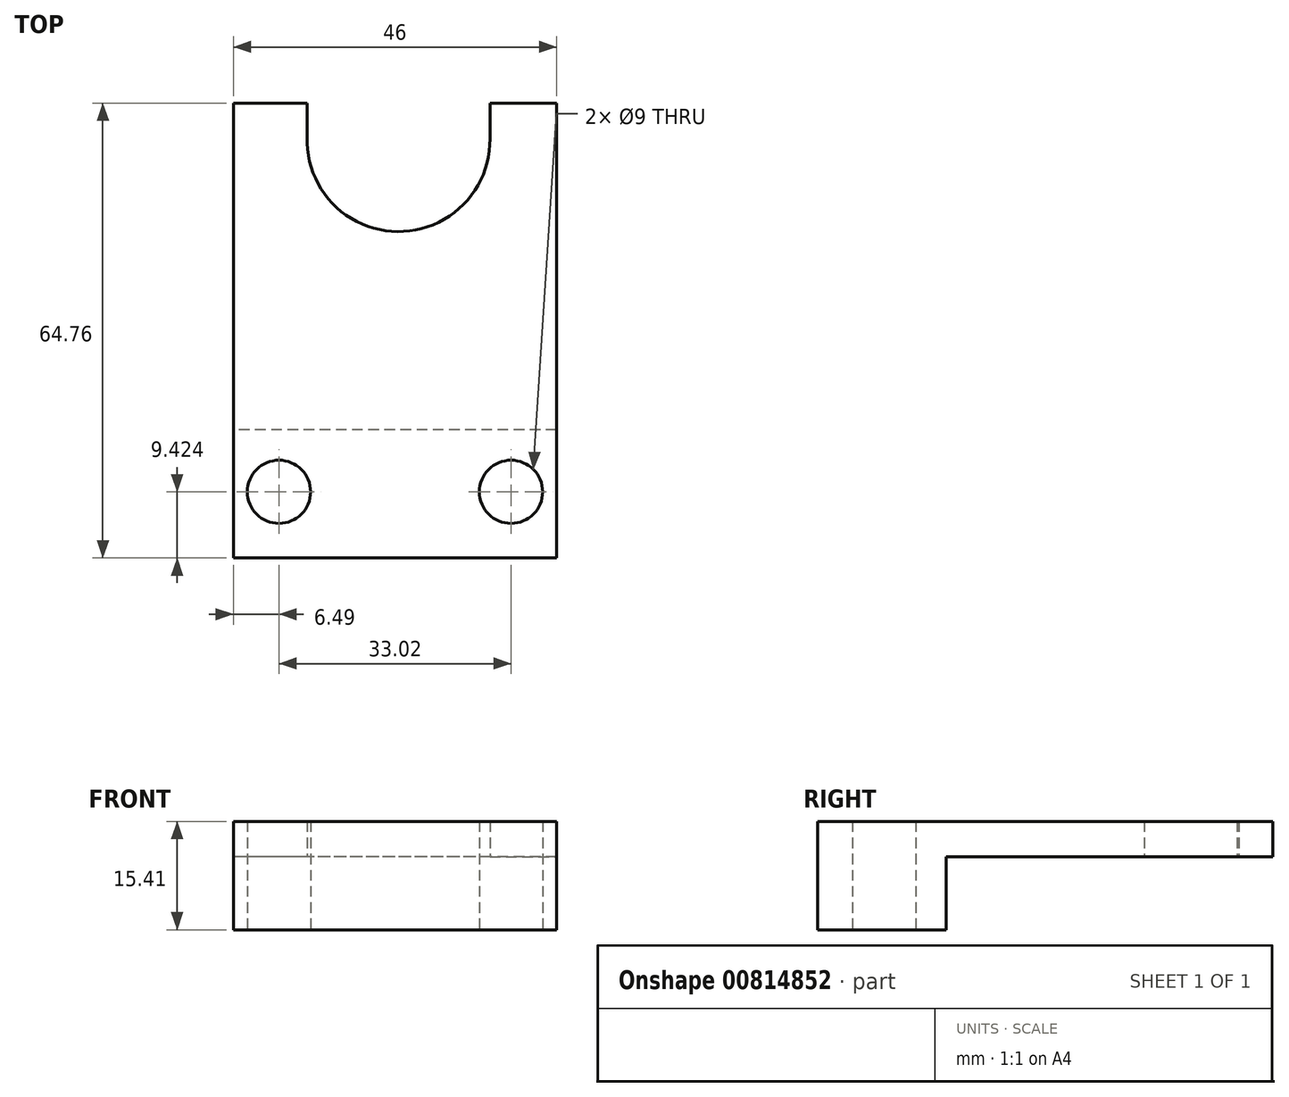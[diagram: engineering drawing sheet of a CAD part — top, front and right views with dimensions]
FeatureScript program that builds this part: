
annotation { "Feature Type Name" : "Feature", "Feature Type Description" : "" }
export const myFeature = defineFeature(function(context is Context, id is Id, definition is map)
    precondition{}
    {
        {
            var Q0;
            Q0=qCreatedBy(makeId("Top.planeOp"),FACE);
            var sketch = newSketch(context, id + "F0", { "sketchPlane" : qUnion([Q0])});
            skLineSegment(sketch, "E0.bottom", {"start": v(23, 53) * mm, "end": v(-23, 53) * mm});
            skLineSegment(sketch, "E0.top", {"start": v(23, -53) * mm, "end": v(-23, -53) * mm});
            skLineSegment(sketch, "E0.left", {"start": v(23, 53) * mm, "end": v(23, -53) * mm});
            skLineSegment(sketch, "E0.right", {"start": v(-23, 53) * mm, "end": v(-23, -53) * mm});
            skPoint(sketch, "E0.middle", {"position": v(0, 0) * mm});
            skArc(sketch, "E1", {"start": v(-1.85, 19.91) * mm, "mid": v(-20, 0.06) * mm, "end": v(-1.97, -19.9) * mm});
            skArc(sketch, "E2", {"start": v(2.22, 19.88) * mm, "mid": v(0.19, 20) * mm, "end": v(-1.85, 19.91) * mm});
            skArc(sketch, "E3", {"start": v(-1.97, -19.9) * mm, "mid": v(0.04, -20) * mm, "end": v(2.05, -19.9) * mm});
            skArc(sketch, "E4", {"start": v(2.05, -19.9) * mm, "mid": v(20, -0.09) * mm, "end": v(2.22, 19.88) * mm});
            skArc(sketch, "E5", {"start": v(-2.06, -20.9) * mm, "mid": v(0, -21) * mm, "end": v(2.06, -20.9) * mm});
            skArc(sketch, "E6", {"start": v(2.06, -20.9) * mm, "mid": v(21, -0.1) * mm, "end": v(2.24, 20.88) * mm});
            skArc(sketch, "E7", {"start": v(-1.88, 20.92) * mm, "mid": v(-21, 0.1) * mm, "end": v(-2.06, -20.9) * mm});
            skArc(sketch, "E8", {"start": v(2.24, 20.88) * mm, "mid": v(0.18, 21) * mm, "end": v(-1.88, 20.92) * mm});
            skLineSegment(sketch, "E9", {"start": v(-1.97, -19.9) * mm, "end": v(-2.06, -20.9) * mm});
            skLineSegment(sketch, "E10", {"start": v(2.05, -19.9) * mm, "end": v(2.06, -20.9) * mm});
            skLineSegment(sketch, "E11", {"start": v(2.24, 20.88) * mm, "end": v(2.22, 19.88) * mm});
            skLineSegment(sketch, "E12", {"start": v(-1.88, 20.92) * mm, "end": v(-1.85, 19.91) * mm});
            skPoint(sketch, "E13", {"position": v(0, -21) * mm});
            skPoint(sketch, "E13.positionSnap0", {"position": v(0, -21) * mm});
            skPoint(sketch, "E14", {"position": v(0.18, 21) * mm});
            skSolve(sketch);
        }
        {
            var Q0;
            Q0=makeQuery(id+"F0.imprint","IMPRINT",FACE,{"disambiguationData":[TD([[makeQuery(id+"F0.imprint","IMPRINT",EDGE,{"derivedFrom":sQuery(id+"F0.wireOp",EDGE,"E1")}),1.0]])]});
            var Q1;
            Q1=makeQuery(id+"F0.imprint","IMPRINT",FACE,{"disambiguationData":[TD([[makeQuery(id+"F0.imprint","IMPRINT",EDGE,{"derivedFrom":sQuery(id+"F0.wireOp",EDGE,"E1")}),-1.0]])]});
            var Q2;
            Q2=makeQuery(id+"F0.imprint","IMPRINT",FACE,{"disambiguationData":[TD([[makeQuery(id+"F0.imprint","IMPRINT",EDGE,{"derivedFrom":sQuery(id+"F0.wireOp",EDGE,"E3")}),-1.0]])]});
            var Q3;
            Q3=makeQuery(id+"F0.imprint","IMPRINT",FACE,{"disambiguationData":[TD([[makeQuery(id+"F0.imprint","IMPRINT",EDGE,{"derivedFrom":sQuery(id+"F0.wireOp",EDGE,"E4")}),-1.0]])]});
            var Q4;
            Q4=makeQuery(id+"F0.imprint","IMPRINT",FACE,{"disambiguationData":[TD([[makeQuery(id+"F0.imprint","IMPRINT",EDGE,{"derivedFrom":sQuery(id+"F0.wireOp",EDGE,"E2")}),-1.0]])]});
            var Q5;
            Q5=makeQuery(id+"F0.imprint","IMPRINT",FACE,{"disambiguationData":[TD([[makeQuery(id+"F0.imprint","IMPRINT",EDGE,{"derivedFrom":sQuery(id+"F0.wireOp",EDGE,"E0.bottom")}),1.0]])]});
            extrude(context, id + "F1", {"entities" : qUnion([Q0, Q1, Q2, Q3, Q4, Q5]), "depth" : 5 * mm, "offsetDistance" : 25.4 * mm});
        }
        {
            var Q0;
            Q0=makeQuery(id+"F0.imprint","IMPRINT",FACE,{"disambiguationData":[TD([[makeQuery(id+"F0.imprint","IMPRINT",EDGE,{"derivedFrom":sQuery(id+"F0.wireOp",EDGE,"E0.bottom")}),1.0]])]});
            var sketch = newSketch(context, id + "F2", { "sketchPlane" : qUnion([Q0])});
            skPoint(sketch, "E15", {"position": v(0, -43) * mm});
            skSolve(sketch);
        }
        {
            var Q0;
            Q0=makeQuery(id+"F0.imprint","IMPRINT",FACE,{"disambiguationData":[TD([[makeQuery(id+"F0.imprint","IMPRINT",EDGE,{"derivedFrom":sQuery(id+"F0.wireOp",EDGE,"E0.bottom")}),1.0]])]});
            var sketch = newSketch(context, id + "F3", { "sketchPlane" : qUnion([Q0])});
            skLineSegment(sketch, "E16", {"start": v(23.01, 22.81) * mm, "end": v(-23.27, 22.81) * mm});
            skSolve(sketch);
        }
        {
            var Q0;
            {var subQ5=makeQuery(id+"F0.imprint","IMPRINT",EDGE,{"derivedFrom":sQuery(id+"F0.wireOp",EDGE,"E0.bottom")});Q0=makeQuery(id+"F3.imprint","IMPRINT",FACE,{"disambiguationData":[TD([[makeQuery(id+"F3.imprint","IMPRINT",EDGE,{"derivedFrom":subQ5}),1.0]])]});}
            extrude(context, id + "F4", {"entities" : qUnion([Q0]), "operationType" : NewBodyOperationType.REMOVE, "depth" : 25.4 * mm, "offsetDistance" : 25.4 * mm});
        }
        {
            var Q0;
            Q0=makeQuery(id+"F2.imprint","IMPRINT",FACE,{"disambiguationData":[TD([[makeQuery(id+"F2.imprint","IMPRINT",EDGE,{"derivedFrom":makeQuery(id+"F0.imprint","IMPRINT",EDGE,{"derivedFrom":sQuery(id+"F0.wireOp",EDGE,"E0.bottom")})}),1.0]])]});
            var sketch = newSketch(context, id + "F5", { "sketchPlane" : qUnion([Q0])});
            skPoint(sketch, "E17", {"position": v(16.51, -43.59) * mm});
            skPoint(sketch, "E18", {"position": v(-16.5, -43.59) * mm});
            skSolve(sketch);
        }
        {
            var Q0;
            Q0=sQuery(id+"F5.wireOp",VERTEX,"E17");
            var Q1;
            Q1=sQuery(id+"F5.wireOp",VERTEX,"E18");
            var Q2;
            Q2=makeQuery(id+"F1.opExtrude","SWEPT_BODY",BODY,{"disambiguationData":[OSD([sQuery(id+"F0.wireOp",EDGE,"E0.bottom"),sQuery(id+"F0.wireOp",EDGE,"E0.top"),sQuery(id+"F0.wireOp",EDGE,"E0.left"),sQuery(id+"F0.wireOp",EDGE,"E0.right")])]});
            hole(context, id + "F6", {"style" : HoleStyle.SIMPLE, "endStyle" : HoleEndStyle.THROUGH, "oppositeDirection" : true, "holeDiameter" : 9 * mm, "majorDiameter" : 6.35 * mm, "isTappedThrough" : true, "tappedDepth" : 12.7 * mm, "tapClearance" : 3, "locations" : qUnion([Q0, Q1]), "scope" : qUnion([Q2])});
        }
        {
            var Q0;
            Q0=makeQuery(id+"F1.opExtrude","CAP_FACE",FACE,{"disambiguationData":[OSD([sQuery(id+"F0.wireOp",EDGE,"E0.bottom"),sQuery(id+"F0.wireOp",EDGE,"E0.top"),sQuery(id+"F0.wireOp",EDGE,"E0.left"),sQuery(id+"F0.wireOp",EDGE,"E0.right")])],"isStart":true});
            var sketch = newSketch(context, id + "F7", { "sketchPlane" : qUnion([Q0])});
            skPoint(sketch, "E19", {"position": v(0.5, 6.5) * mm});
            skPoint(sketch, "E20", {"position": v(0.5, 0.03) * mm});
            skPoint(sketch, "E21", {"position": v(0.5, -6.45) * mm});
            skSolve(sketch);
        }
        {
            var Q0;
            Q0=sQuery(id+"F7.wireOp",VERTEX,"E21");
            var Q1;
            Q1=makeQuery(id+"F1.opExtrude","SWEPT_BODY",BODY,{"disambiguationData":[OSD([sQuery(id+"F0.wireOp",EDGE,"E0.bottom"),sQuery(id+"F0.wireOp",EDGE,"E0.top"),sQuery(id+"F0.wireOp",EDGE,"E0.left"),sQuery(id+"F0.wireOp",EDGE,"E0.right")])]});
            hole(context, id + "F8", {"style" : HoleStyle.SIMPLE, "endStyle" : HoleEndStyle.THROUGH, "holeDiameter" : 26 * mm, "majorDiameter" : 6.35 * mm, "isTappedThrough" : true, "tappedDepth" : 12.7 * mm, "tapClearance" : 3, "locations" : qUnion([Q0]), "scope" : qUnion([Q1])});
        }
        {
            var Q0;
            Q0=makeQuery(id+"F1.opExtrude","CAP_FACE",FACE,{"disambiguationData":[OSD([sQuery(id+"F0.wireOp",EDGE,"E0.bottom"),sQuery(id+"F0.wireOp",EDGE,"E0.top"),sQuery(id+"F0.wireOp",EDGE,"E0.left"),sQuery(id+"F0.wireOp",EDGE,"E0.right")])],"isStart":true});
            var sketch = newSketch(context, id + "F9", { "sketchPlane" : qUnion([Q0])});
            skLineSegment(sketch, "E22.bottom", {"start": v(23, 34.76) * mm, "end": v(-23, 34.76) * mm});
            skLineSegment(sketch, "E22.top", {"start": v(23, 53) * mm, "end": v(-23, 53) * mm});
            skLineSegment(sketch, "E22.left", {"start": v(23, 34.76) * mm, "end": v(23, 53) * mm});
            skLineSegment(sketch, "E22.right", {"start": v(-23, 34.76) * mm, "end": v(-23, 53) * mm});
            skSolve(sketch);
        }
        {
            var Q0;
            Q0=makeQuery(id+"F9.imprint","IMPRINT",FACE,{"disambiguationData":[TD([[makeQuery(id+"F9.imprint","IMPRINT",EDGE,{"derivedFrom":sQuery(id+"F9.wireOp",EDGE,"E22.bottom")}),-1.0]])]});
            extrude(context, id + "F10", {"entities" : qUnion([Q0]), "operationType" : NewBodyOperationType.ADD, "depth" : 10.4 * mm, "offsetDistance" : 25.4 * mm});
        }
        {
            var Q0;
            Q0=makeQuery(id+"F1.opExtrude","CAP_FACE",FACE,{"disambiguationData":[OSD([sQuery(id+"F0.wireOp",EDGE,"E0.bottom"),sQuery(id+"F0.wireOp",EDGE,"E0.top"),sQuery(id+"F0.wireOp",EDGE,"E0.left"),sQuery(id+"F0.wireOp",EDGE,"E0.right")])],"isStart":true});
            var sketch = newSketch(context, id + "F11", { "sketchPlane" : qUnion([Q0])});
            skLineSegment(sketch, "E23", {"start": v(0.01, 6.54) * mm, "end": v(0.01, -11.75) * mm});
            skLineSegment(sketch, "E24", {"start": v(0.01, -11.75) * mm, "end": v(-23, -11.75) * mm});
            skLineSegment(sketch, "E25", {"start": v(-23, -11.75) * mm, "end": v(23, -11.75) * mm});
            skLineSegment(sketch, "E26", {"start": v(23, -11.75) * mm, "end": v(23, -22.81) * mm});
            skLineSegment(sketch, "E27", {"start": v(23, -22.81) * mm, "end": v(-23, -22.81) * mm});
            skLineSegment(sketch, "E28", {"start": v(-23, -22.81) * mm, "end": v(-23, -11.75) * mm});
            skSolve(sketch);
        }
        {
            var Q0;
            {var subQ0=sQuery(id+"F11.wireOp",EDGE,"E26");Q0=makeQuery(id+"F11.imprint","IMPRINT",FACE,{"disambiguationData":[TD([[makeQuery(id+"F11.imprint","IMPRINT",EDGE,{"derivedFrom":subQ0}),1.0]])]});}
            extrude(context, id + "F12", {"entities" : qUnion([Q0]), "operationType" : NewBodyOperationType.REMOVE, "oppositeDirection" : true, "depth" : 25.4 * mm, "offsetDistance" : 25.4 * mm});
        }
        {
            var Q0;
            Q0=makeQuery(id+"F1.opExtrude","CAP_FACE",FACE,{"disambiguationData":[OSD([sQuery(id+"F0.wireOp",EDGE,"E0.bottom"),sQuery(id+"F0.wireOp",EDGE,"E0.top"),sQuery(id+"F0.wireOp",EDGE,"E0.left"),sQuery(id+"F0.wireOp",EDGE,"E0.right")])],"isStart":true});
            var sketch = newSketch(context, id + "F13", { "sketchPlane" : qUnion([Q0])});
            skLineSegment(sketch, "E29", {"start": v(-12.5, -5.99) * mm, "end": v(-12.5, -11.75) * mm});
            skLineSegment(sketch, "E30", {"start": v(13.5, -6.24) * mm, "end": v(13.5, -11.75) * mm});
            skSolve(sketch);
        }
        {
            var Q0;
            {var subQ0=sQuery(id+"F13.wireOp",EDGE,"E30");var subQ1=makeQuery(id+"F12.boolean.opBoolean","COPY",EDGE,{"derivedFrom":makeQuery(id+"F12.opExtrude","CAP_EDGE",EDGE,{"disambiguationData":[OSD([sQuery(id+"F11.wireOp",EDGE,"E25")])],"isStart":true})});var subQ2=makeQuery(id+"F13.imprint","INTERSECT",VERTEX,{"derivedFrom":[subQ1,subQ0]});Q0=makeQuery(id+"F13.imprint","IMPRINT",FACE,{"disambiguationData":[TD([[makeQuery(id+"F13.imprint","IMPRINT",EDGE,{"disambiguationData":[TD([[subQ2,1.0]])],"derivedFrom":subQ0}),-1.0]])]});}
            var Q1;
            {var subQ0=sQuery(id+"F13.wireOp",EDGE,"E29");var subQ1=makeQuery(id+"F12.boolean.opBoolean","COPY",EDGE,{"derivedFrom":makeQuery(id+"F12.opExtrude","CAP_EDGE",EDGE,{"disambiguationData":[OSD([sQuery(id+"F11.wireOp",EDGE,"E24")])],"isStart":true})});var subQ2=makeQuery(id+"F13.imprint","INTERSECT",VERTEX,{"derivedFrom":[subQ1,subQ0]});Q1=makeQuery(id+"F13.imprint","IMPRINT",FACE,{"disambiguationData":[TD([[makeQuery(id+"F13.imprint","IMPRINT",EDGE,{"disambiguationData":[TD([[subQ2,1.0]])],"derivedFrom":subQ0}),1.0]])]});}
            extrude(context, id + "F14", {"entities" : qUnion([Q0, Q1]), "operationType" : NewBodyOperationType.REMOVE, "oppositeDirection" : true, "depth" : 25.4 * mm, "offsetDistance" : 25.4 * mm});
        }
    });
